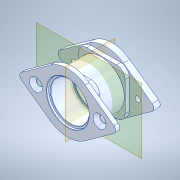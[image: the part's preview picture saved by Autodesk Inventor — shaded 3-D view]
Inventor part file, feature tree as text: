
AUTODESK INVENTOR PART (.ipt)
format: ipt  version: 2020 (Build 240168000, 168)  size: 229,376 bytes
history: native  units: in
note: dims shown in document units (in); Inventor stores cm internally (conversion verified against a paired STEP export)
features: other x2, plane x1
ambient origin geometry x8: Origin, YZ Plane, XZ Plane, XY Plane, X Axis, Y Axis, Z Axis, Center Point
bodies: Solid1 (feature_tree), Solid2 (feature_tree)
feature tree (3):
  plane  "Work Plane1"
  other  "217-3436-001 Rev2_1:1"
  other  "217-3436-002 Rev2_2:1"
